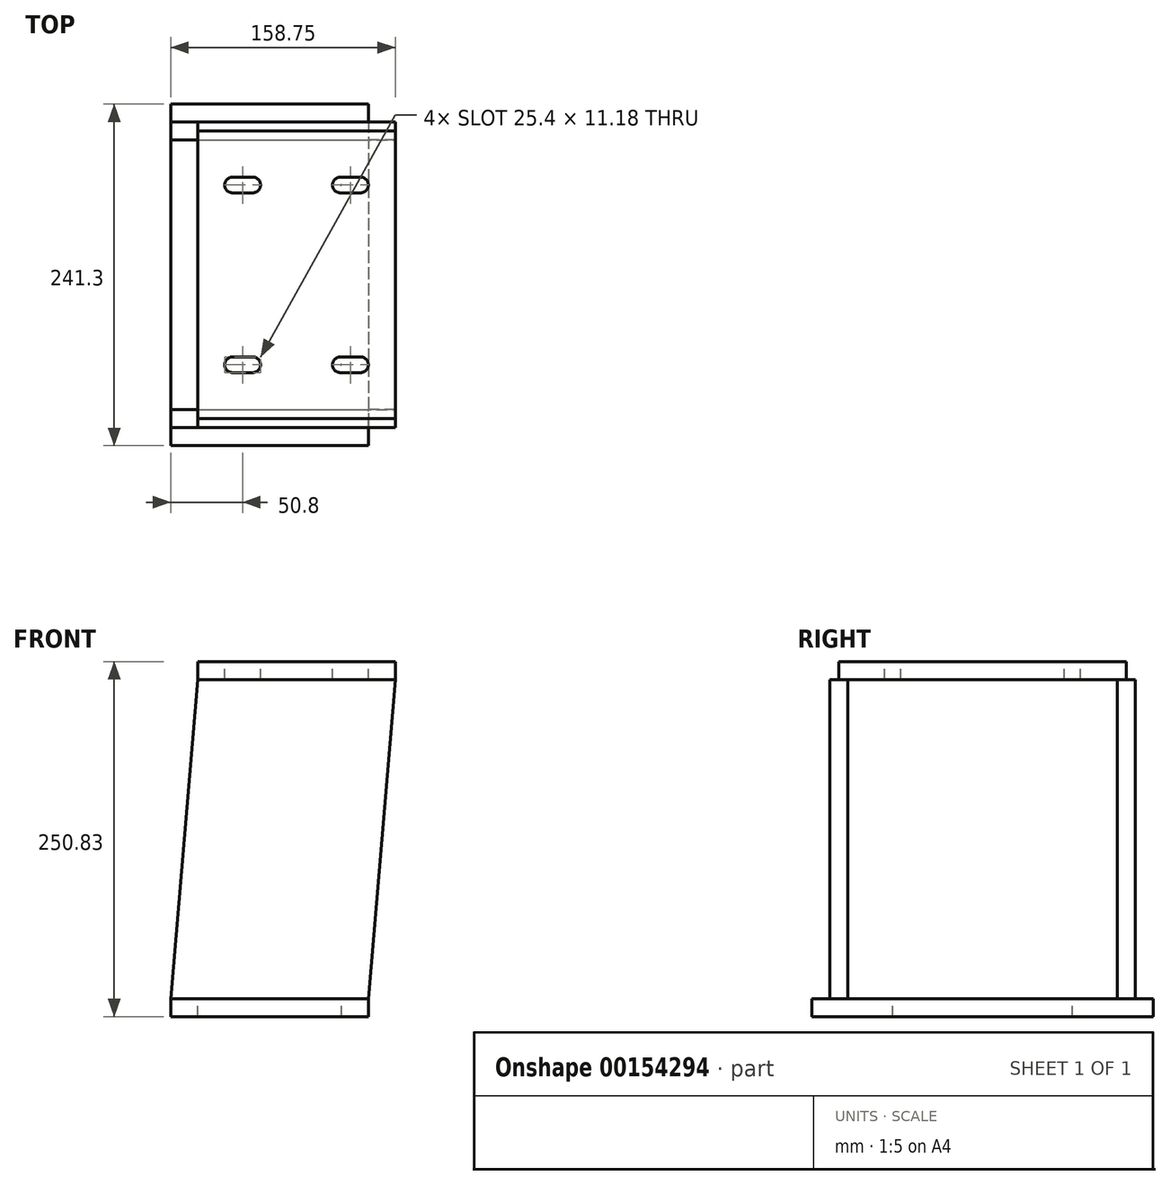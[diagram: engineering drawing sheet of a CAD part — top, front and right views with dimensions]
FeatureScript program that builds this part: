
annotation { "Feature Type Name" : "Feature", "Feature Type Description" : "" }
export const myFeature = defineFeature(function(context is Context, id is Id, definition is map)
    precondition{}
    {
        {
            var Q0;
            Q0=qCreatedBy(makeId("Top.planeOp"),FACE);
            cPlane(context, id + "F0", {"entities" : qUnion([Q0]), "cplaneType" : CPlaneType.OFFSET, "offset" : 250.82 * mm, "width" : 152.4 * mm, "height" : 152.4 * mm});
        }
        {
            var Q0;
            Q0=qCreatedBy(makeId("Top.planeOp"),FACE);
            var sketch = newSketch(context, id + "F1", { "sketchPlane" : qUnion([Q0])});
            skLineSegment(sketch, "E0.bottom", {"start": v(-69.85, 120.65) * mm, "end": v(69.85, 120.65) * mm});
            skLineSegment(sketch, "E0.top", {"start": v(-69.85, -120.65) * mm, "end": v(69.85, -120.65) * mm});
            skLineSegment(sketch, "E0.left", {"start": v(-69.85, 120.65) * mm, "end": v(-69.85, -120.65) * mm});
            skLineSegment(sketch, "E0.right", {"start": v(69.85, 120.65) * mm, "end": v(69.85, -120.65) * mm});
            skPoint(sketch, "E0.middle", {"position": v(0, 0) * mm});
            skSolve(sketch);
        }
        {
            var Q0;
            Q0=qSketchRegion(id+"F1",true);
            extrude(context, id + "F2", {"entities" : qUnion([Q0]), "depth" : 12.7 * mm});
        }
        {
            var Q0;
            Q0=makeQuery(id+"F2.opExtrude","CAP_FACE",FACE,{"disambiguationData":[OSD([sQuery(id+"F1.wireOp",EDGE,"E0.bottom"),sQuery(id+"F1.wireOp",EDGE,"E0.top"),sQuery(id+"F1.wireOp",EDGE,"E0.left"),sQuery(id+"F1.wireOp",EDGE,"E0.right")])],"isStart":false});
            var sketch = newSketch(context, id + "F3", { "sketchPlane" : qUnion([Q0])});
            skLineSegment(sketch, "E1.0", {"start": v(69.85, 120.65) * mm, "end": v(69.85, -120.65) * mm, "construction": true});
            skLineSegment(sketch, "E2.0", {"start": v(50.8, 120.65) * mm, "end": v(50.8, -120.65) * mm, "construction": true});
            skLineSegment(sketch, "E3.0", {"start": v(-50.8, 120.65) * mm, "end": v(-50.8, -120.65) * mm, "construction": true});
            skLineSegment(sketch, "E4", {"start": v(-147.29, 0) * mm, "end": v(150.02, 0) * mm, "construction": true});
            skLineSegment(sketch, "E5.0", {"start": v(-147.29, -63.5) * mm, "end": v(150.02, -63.5) * mm, "construction": true});
            skLineSegment(sketch, "E6.MirrorCS", {"start": v(-147.29, 63.5) * mm, "end": v(150.02, 63.5) * mm, "construction": true});
            skPoint(sketch, "E7", {"position": v(-50.8, 63.5) * mm});
            skPoint(sketch, "E8", {"position": v(50.8, 63.5) * mm});
            skPoint(sketch, "E9", {"position": v(50.8, -63.5) * mm});
            skPoint(sketch, "E10", {"position": v(-50.8, -63.5) * mm});
            skSolve(sketch);
        }
        {
            var Q0;
            Q0=sQuery(id+"F3.wireOp",VERTEX,"E7");
            var Q1;
            Q1=sQuery(id+"F3.wireOp",VERTEX,"E8");
            var Q2;
            Q2=sQuery(id+"F3.wireOp",VERTEX,"E9");
            var Q3;
            Q3=sQuery(id+"F3.wireOp",VERTEX,"E10");
            var Q4;
            Q4=makeQuery(id+"F2.opExtrude","SWEPT_BODY",BODY,{"disambiguationData":[OSD([sQuery(id+"F1.wireOp",EDGE,"E0.bottom"),sQuery(id+"F1.wireOp",EDGE,"E0.top"),sQuery(id+"F1.wireOp",EDGE,"E0.left"),sQuery(id+"F1.wireOp",EDGE,"E0.right")])]});
            hole(context, id + "F4", {"style" : HoleStyle.SIMPLE, "endStyle" : HoleEndStyle.THROUGH, "standardTappedOrClearance" : lookupTablePath({ "standard" : "ANSI", "size" : "9/16 (0.56)", "type" : "Drilled" }), "standardBlindInLast" : lookupTablePath({ "standard" : "ANSI", "size" : "9/16", "type" : "Drilled" }), "holeDiameter" : 9 / 406.4 * mm, "locations" : qUnion([Q0, Q1, Q2, Q3]), "scope" : qUnion([Q4]), "isTappedThrough" : true});
        }
        {
            var Q0;
            Q0=qCreatedBy(id+"F0.planeOp",FACE);
            var sketch = newSketch(context, id + "F5", { "sketchPlane" : qUnion([Q0])});
            skLineSegment(sketch, "E11", {"start": v(0, 141.47) * mm, "end": v(0, -163.23) * mm, "construction": true});
            skLineSegment(sketch, "E12", {"start": v(-208.48, 0) * mm, "end": v(177.55, 0) * mm, "construction": true});
            skLineSegment(sketch, "E13.0", {"start": v(19.05, 141.47) * mm, "end": v(19.05, -163.23) * mm, "construction": true});
            skLineSegment(sketch, "E14.bottom", {"start": v(-50.8, 101.6) * mm, "end": v(88.9, 101.6) * mm});
            skLineSegment(sketch, "E14.top", {"start": v(-50.8, -101.6) * mm, "end": v(88.9, -101.6) * mm});
            skLineSegment(sketch, "E14.left", {"start": v(-50.8, 101.6) * mm, "end": v(-50.8, -101.6) * mm});
            skLineSegment(sketch, "E14.right", {"start": v(88.9, 101.6) * mm, "end": v(88.9, -101.6) * mm});
            skPoint(sketch, "E14.middle", {"position": v(19.05, 0) * mm});
            skSolve(sketch);
        }
        {
            var Q0;
            Q0=qSketchRegion(id+"F5",true);
            extrude(context, id + "F6", {"entities" : qUnion([Q0]), "oppositeDirection" : true, "depth" : 12.7 * mm});
        }
        {
            var Q0;
            Q0=makeQuery(id+"F6.opExtrude","CAP_FACE",FACE,{"disambiguationData":[OSD([sQuery(id+"F5.wireOp",EDGE,"E14.bottom"),sQuery(id+"F5.wireOp",EDGE,"E14.top"),sQuery(id+"F5.wireOp",EDGE,"E14.left"),sQuery(id+"F5.wireOp",EDGE,"E14.right")])],"isStart":true});
            var sketch = newSketch(context, id + "F7", { "sketchPlane" : qUnion([Q0])});
            skLineSegment(sketch, "E15", {"start": v(-136.74, 0) * mm, "end": v(178.27, 0) * mm, "construction": true});
            skPoint(sketch, "E15.endSnap0", {"position": v(-50.8, 0) * mm});
            skLineSegment(sketch, "E16", {"start": v(19.05, 101.6) * mm, "end": v(19.05, -101.6) * mm, "construction": true});
            skLineSegment(sketch, "E17.0", {"start": v(-19.05, 101.6) * mm, "end": v(-19.05, -101.6) * mm, "construction": true});
            skLineSegment(sketch, "E18.0", {"start": v(-136.74, -63.5) * mm, "end": v(-26.16, -63.5) * mm, "construction": true});
            skLineSegment(sketch, "E19.0", {"start": v(-26.16, 101.6) * mm, "end": v(-26.16, -101.6) * mm, "construction": true});
            skLineSegment(sketch, "E20.MirrorCS", {"start": v(-11.94, 101.6) * mm, "end": v(-11.94, -101.6) * mm, "construction": true});
            skLineSegment(sketch, "E21.trimOffspring", {"start": v(-11.94, -63.5) * mm, "end": v(178.27, -63.5) * mm, "construction": true});
            skLineSegment(sketch, "E22", {"start": v(-26.16, -63.5) * mm, "end": v(-11.94, -63.5) * mm});
            skArc(sketch, "E23.0.startCap", {"start": v(-26.16, -69.09) * mm, "mid": v(-31.75, -63.5) * mm, "end": v(-26.16, -57.91) * mm});
            skArc(sketch, "E23.0.endCap", {"start": v(-11.94, -57.91) * mm, "mid": v(-6.35, -63.5) * mm, "end": v(-11.94, -69.09) * mm});
            skLineSegment(sketch, "E23.0.left", {"start": v(-26.16, -57.91) * mm, "end": v(-11.94, -57.91) * mm});
            skLineSegment(sketch, "E23.0.right", {"start": v(-26.16, -69.09) * mm, "end": v(-11.94, -69.09) * mm});
            skLineSegment(sketch, "E24.MirrorCS", {"start": v(64.26, -69.09) * mm, "end": v(50.04, -69.09) * mm});
            skLineSegment(sketch, "E25.MirrorCS", {"start": v(64.26, -57.91) * mm, "end": v(50.04, -57.91) * mm});
            skArc(sketch, "E26.MirrorCS", {"start": v(50.04, -57.91) * mm, "mid": v(44.45, -63.5) * mm, "end": v(50.04, -69.09) * mm});
            skArc(sketch, "E27.MirrorCS", {"start": v(64.26, -69.09) * mm, "mid": v(69.85, -63.5) * mm, "end": v(64.26, -57.91) * mm});
            skLineSegment(sketch, "E28.MirrorCS", {"start": v(64.26, -63.5) * mm, "end": v(50.04, -63.5) * mm});
            skLineSegment(sketch, "E29.MirrorCS", {"start": v(64.26, 69.09) * mm, "end": v(50.04, 69.09) * mm});
            skLineSegment(sketch, "E30.MirrorCS", {"start": v(-26.16, 69.09) * mm, "end": v(-11.94, 69.09) * mm});
            skLineSegment(sketch, "E31.MirrorCS", {"start": v(-26.16, 57.91) * mm, "end": v(-11.94, 57.91) * mm});
            skArc(sketch, "E32.MirrorCS", {"start": v(-11.94, 57.91) * mm, "mid": v(-6.35, 63.5) * mm, "end": v(-11.94, 69.09) * mm});
            skArc(sketch, "E33.MirrorCS", {"start": v(-26.16, 69.09) * mm, "mid": v(-31.75, 63.5) * mm, "end": v(-26.16, 57.91) * mm});
            skLineSegment(sketch, "E34.MirrorCS", {"start": v(-26.16, 63.5) * mm, "end": v(-11.94, 63.5) * mm});
            skLineSegment(sketch, "E35.MirrorCS", {"start": v(64.26, 63.5) * mm, "end": v(50.04, 63.5) * mm});
            skLineSegment(sketch, "E36.MirrorCS", {"start": v(64.26, 57.91) * mm, "end": v(50.04, 57.91) * mm});
            skArc(sketch, "E37.MirrorCS", {"start": v(50.04, 57.91) * mm, "mid": v(44.45, 63.5) * mm, "end": v(50.04, 69.09) * mm});
            skArc(sketch, "E38.MirrorCS", {"start": v(64.26, 69.09) * mm, "mid": v(69.85, 63.5) * mm, "end": v(64.26, 57.91) * mm});
            skSolve(sketch);
        }
        {
            var Q0;
            Q0=qSketchRegion(id+"F7",true);
            extrude(context, id + "F8", {"entities" : qUnion([Q0]), "operationType" : NewBodyOperationType.REMOVE, "oppositeDirection" : true, "depth" : 25.4 * mm});
        }
        {
            var Q0;
            Q0=makeQuery(id+"F6.opExtrude","SWEPT_FACE",FACE,{"disambiguationData":[OSD([sQuery(id+"F5.wireOp",EDGE,"E14.top")])]});
            var sketch = newSketch(context, id + "F9", { "sketchPlane" : qUnion([Q0])});
            skLineSegment(sketch, "E39.0", {"start": v(-50.8, 238.13) * mm, "end": v(88.9, 238.13) * mm});
            skLineSegment(sketch, "E40.0", {"start": v(-69.85, 12.7) * mm, "end": v(69.85, 12.7) * mm});
            skLineSegment(sketch, "E41", {"start": v(-50.8, 238.13) * mm, "end": v(-69.85, 12.7) * mm});
            skLineSegment(sketch, "E42", {"start": v(88.9, 238.13) * mm, "end": v(69.85, 12.7) * mm});
            skSolve(sketch);
        }
        {
            var Q0;
            Q0=qSketchRegion(id+"F9",true);
            extrude(context, id + "F10", {"entities" : qUnion([Q0]), "endBound" : BoundingType.SYMMETRIC, "depth" : 12.7 * mm});
        }
        {
            var Q0;
            Q0=makeQuery(id+"F10.opExtrude","SWEPT_BODY",BODY,{"disambiguationData":[OSD([sQuery(id+"F9.wireOp",EDGE,"E39.0"),sQuery(id+"F9.wireOp",EDGE,"E40.0"),sQuery(id+"F9.wireOp",EDGE,"E41"),sQuery(id+"F9.wireOp",EDGE,"E42")])]});
            var Q1;
            Q1=qCreatedBy(makeId("Front.planeOp"),FACE);
            mirror(context, id + "F11", {"entities" : qUnion([Q0]), "mirrorPlane" : qUnion([Q1])});
        }
    });
